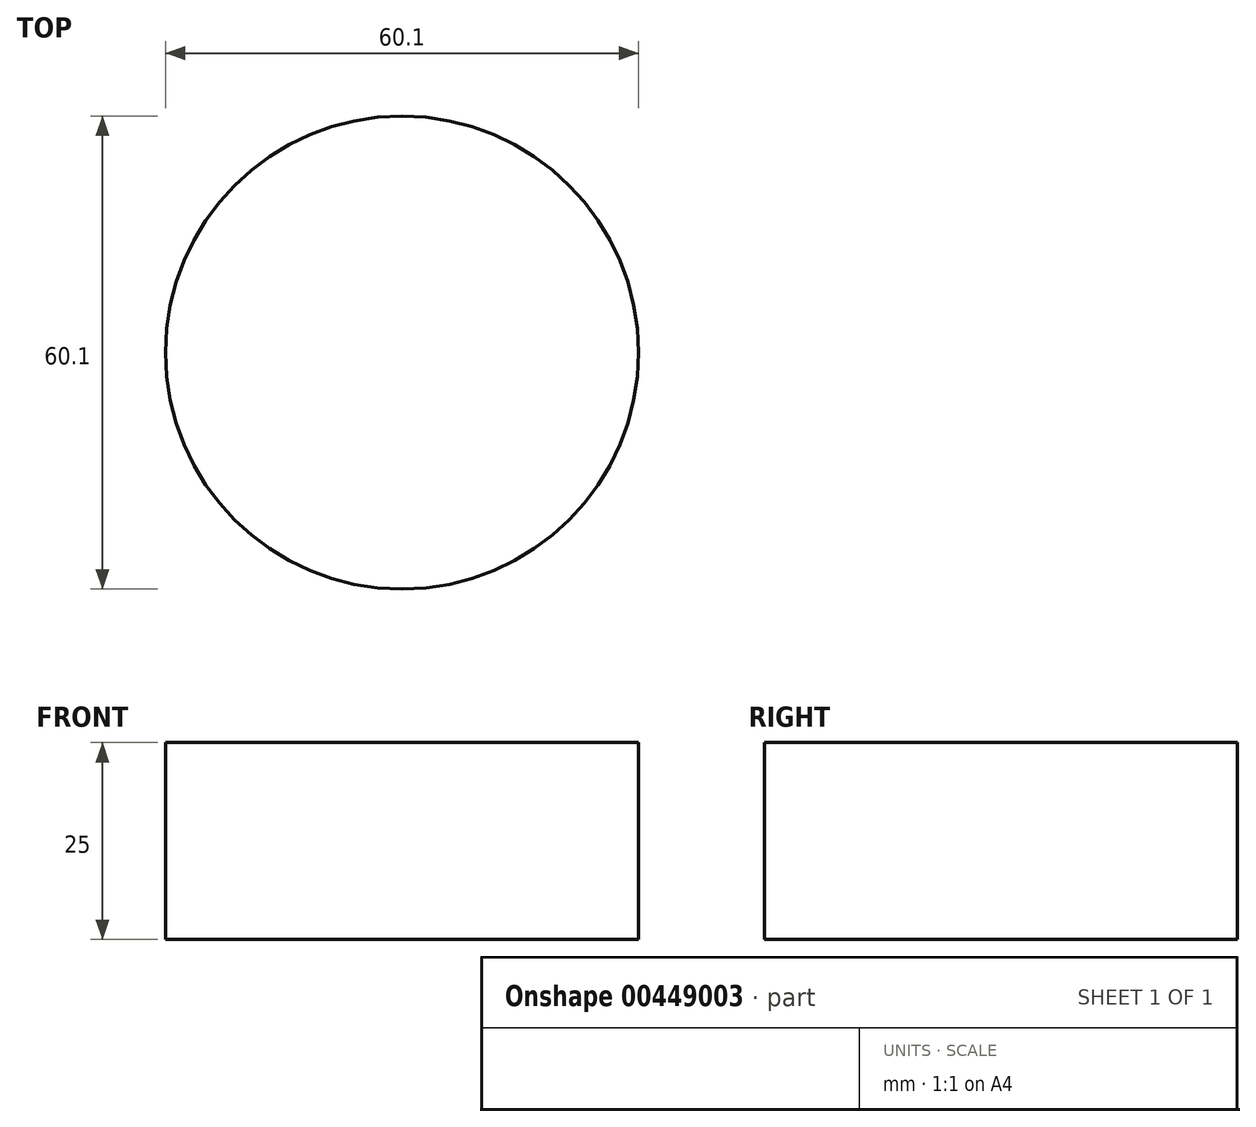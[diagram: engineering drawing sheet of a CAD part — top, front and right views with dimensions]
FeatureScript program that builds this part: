
annotation { "Feature Type Name" : "Feature", "Feature Type Description" : "" }
export const myFeature = defineFeature(function(context is Context, id is Id, definition is map)
    precondition{}
    {
        {
            var Q0;
            Q0=qCreatedBy(makeId("Top.planeOp"),FACE);
            var sketch = newSketch(context, id + "F0", { "sketchPlane" : qUnion([Q0])});
            skCircle(sketch, "E0", {"center": v(0, 0) * mm, "radius": 30.05 * mm});
            skSolve(sketch);
        }
        {
            var Q0;
            Q0=qSketchRegion(id+"F0",true);
            extrude(context, id + "F1", {"entities" : qUnion([Q0]), "endBound" : BoundingType.SYMMETRIC, "depth" : 25 * mm});
        }
    });
